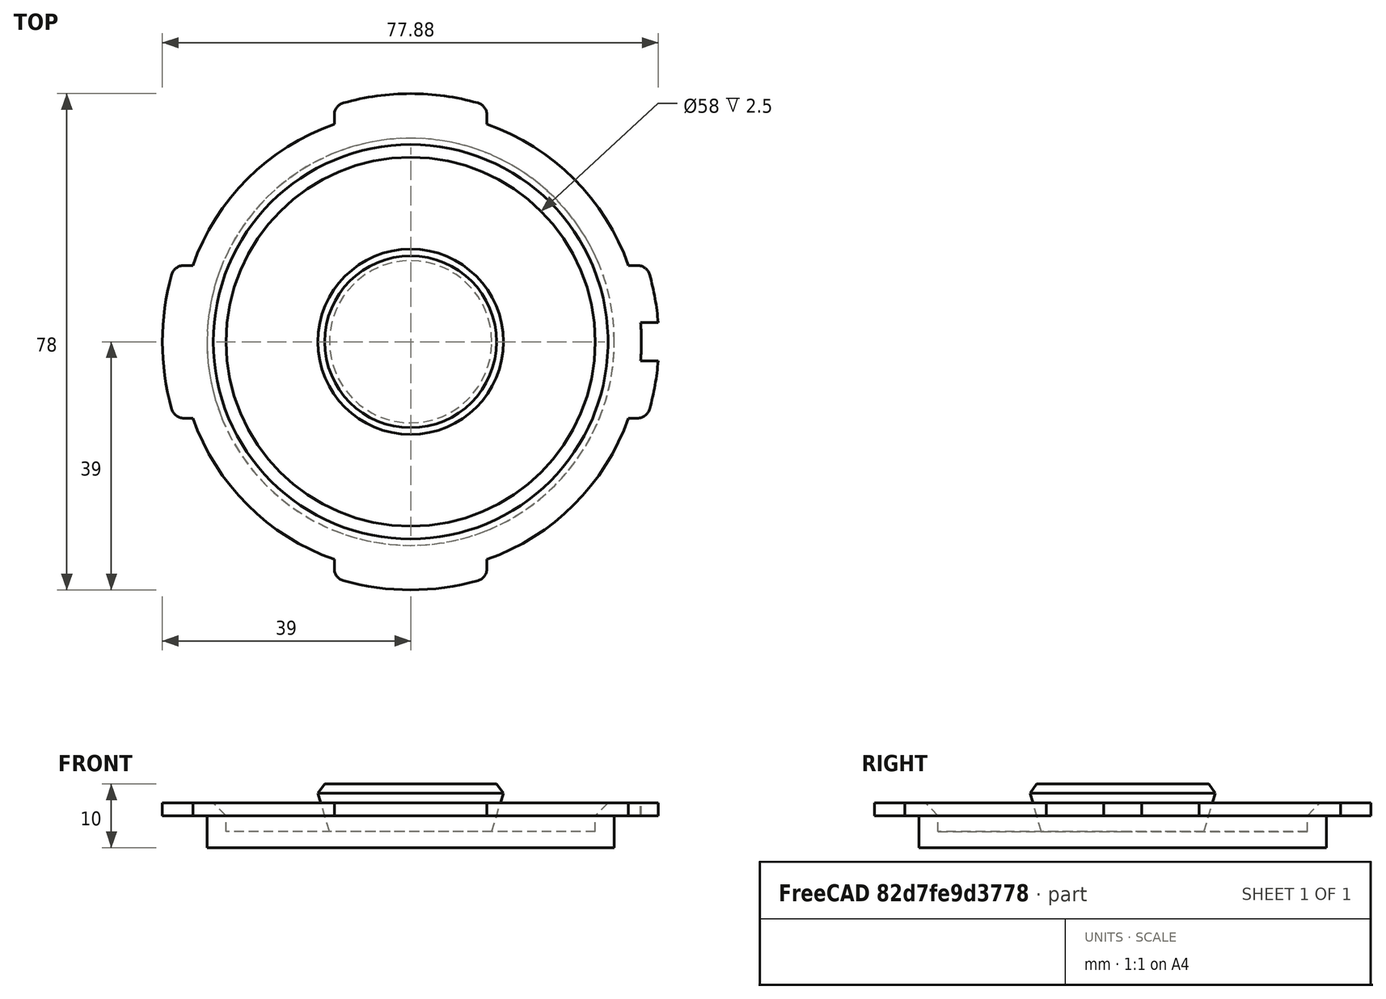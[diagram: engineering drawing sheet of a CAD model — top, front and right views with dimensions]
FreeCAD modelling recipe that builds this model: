
FCSTD DOCUMENT  (FreeCAD 0.18R4 (GitTag))
Label: oct19-body-port-cover
License: All rights reserved
LicenseURL: http://en.wikipedia.org/wiki/All_rights_reserved
objects: Part::Cylinder×6, Part::Box×5, Part::Cut×5, Part::Fillet×4, Part::MultiFuse×4, Part::Fuse×2, Part::Chamfer×2, TechDraw::DrawViewDraft×2, Part::Cone×1, TechDraw::DrawSVGTemplate×1, TechDraw::DrawViewPart×1, TechDraw::DrawViewDimension×1, TechDraw::DrawPage×1
note: 29 computed .brp shape members not serialized (recipe doc carries the construction recipe); baked Part::Feature solids carry a one-line shape summary decoded from their .brp

FEATURE [Part::Cylinder] Cylinder
  Angle = 360
  AttacherType = Attacher::AttachEngine3D
  Height = 7
  Radius = 32
FEATURE [Part::Cylinder] Cylinder001
  Angle = 360
  AttacherType = Attacher::AttachEngine3D
  Height = 2
  Placement = pos=(0,0,5) rot=(0,0,1;0rad)
  Radius = 36.25
FEATURE [Part::Cylinder] Cylinder003
  Angle = 360
  AttacherType = Attacher::AttachEngine3D
  Height = 2
  Placement = pos=(0,0,5) rot=(0,0,1;0rad)
  Radius = 39
FEATURE [Part::Box] Box  label="Cube"
  AttacherType = Attacher::AttachEngine3D
  Height = 10
  Length = 100
  Placement = pos=(-50,12,0) rot=(0,0,1;0rad)
  Width = 40
FEATURE [Part::Box] Box001  label="Cube001"
  AttacherType = Attacher::AttachEngine3D
  Height = 10
  Length = 100
  Placement = pos=(-50,-52,0) rot=(0,0,1;0rad)
  Width = 40
FEATURE [Part::Fuse] Fusion
  Base = -> Box
  Tool = -> Box001
FEATURE [Part::Cut] Cut
  Base = -> Cylinder003
  Tool = -> Fusion
FEATURE [Part::Fillet] Fillet
  Base = -> Cut
  Edges = 2 edges r=2: [Edge3,Edge6]
FEATURE [Part::Fillet] Fillet001
  Base = -> Fillet
  Edges = 2 edges r=2: [Edge19,Edge21]
FEATURE [Part::Box] Box002  label="Cube002"
  AttacherType = Attacher::AttachEngine3D
  Height = 10
  Length = 100
  Placement = pos=(-50,-52,0) rot=(0,0,1;0rad)
  Width = 40
FEATURE [Part::Box] Box003  label="Cube003"
  AttacherType = Attacher::AttachEngine3D
  Height = 10
  Length = 100
  Placement = pos=(-50,12,0) rot=(0,0,1;0rad)
  Width = 40
FEATURE [Part::Fuse] Fusion001
  Base = -> Box003
  Tool = -> Box002
FEATURE [Part::Cylinder] Cylinder004
  Angle = 360
  AttacherType = Attacher::AttachEngine3D
  Height = 2
  Placement = pos=(0,0,5) rot=(0,0,1;0rad)
  Radius = 39
FEATURE [Part::Cut] Cut001
  Base = -> Cylinder004
  Tool = -> Fusion001
FEATURE [Part::Fillet] Fillet003
  Base = -> Cut001
  Edges = 2 edges r=2: [Edge3,Edge6]
FEATURE [Part::Fillet] Fillet002
  Base = -> Fillet003
  Edges = 2 edges r=2: [Edge19,Edge21]
  Placement = pos=(0,0,0) rot=(0,0,1;1.5708rad)
FEATURE [Part::Box] Box004  label="Cube004"
  AttacherType = Attacher::AttachEngine3D
  Height = 10
  Length = 10
  Placement = pos=(36,-3,0) rot=(0,0,1;0rad)
  Width = 6
FEATURE [Part::Cut] Cut002
  Base = -> Fillet001
  Tool = -> Box004
FEATURE [Part::MultiFuse] Fusion002  label="Bayonet"
  Shapes = -> [Fillet002,Cut002]
FEATURE [Part::Cylinder] Cylinder005
  Angle = 360
  AttacherType = Attacher::AttachEngine3D
  Height = 7
  Placement = pos=(0,0,2.5) rot=(0,0,1;0rad)
  Radius = 29
FEATURE [Part::Cylinder] Cylinder006
  Angle = 360
  AttacherType = Attacher::AttachEngine3D
  Height = 7
  Placement = pos=(0,0,4) rot=(0,0,1;0rad)
  Radius = 31
FEATURE [Part::MultiFuse] Fusion003
  Shapes = -> [Cylinder,Fusion002]
FEATURE [Part::MultiFuse] Fusion004
  Shapes = -> [Cylinder001,Fusion003]
FEATURE [Part::Cut] Cut003
  Base = -> Fusion004
  Tool = -> Cylinder005
FEATURE [Part::Chamfer] Chamfer
  Base = -> Cylinder006
  Edges = 1 edges r=3: [Edge3]
FEATURE [Part::Cut] Cut004
  Base = -> Cut003
  Tool = -> Chamfer
FEATURE [Part::Cone] Cone
  Angle = 360
  AttacherType = Attacher::AttachEngine3D
  Height = 10
  Radius1 = 12
  Radius2 = 15
FEATURE [Part::Chamfer] Chamfer001  label="Handle"
  Base = -> Cone
  Edges = 1 edges r=1.5: [Edge1]
FEATURE [Part::MultiFuse] Fusion005  label="oct19-body-port-cover"
  Shapes = -> [Cut004,Chamfer001]
FEATURE [TechDraw::DrawSVGTemplate] Template
  EditableTexts = APPROVER_NAME=APPROVER NAME; AUTHOR_NAME=AUTHOR NAME; DATE=YYYY-MM-DD; DN=DN; OWNER_NAME=OWNER NAME; PM=PM; PN=PN; REVISION=REV A; RIGHTS=(R) DO NOT DUPLICATE THIS DRAWING TO THIRD PARTIES WITHOUT OWNER'S PERMISSION !; SCALE=M x:x; SHEET=99 of 99; SIZE=A4; TITLELINE-1=FreeCAD; TOLERANCE=+/- ?
  Height = 210
  Orientation = 1
  Width = 297
FEATURE [TechDraw::DrawViewDraft] DraftView  label="Front"
  Direction = (0,0,1)
  FontSize = 12
  LineSpacing = 1
  LineStyle = Solie
  LineWidth = 0.35
  LockPosition = false
  Rotation = 0
  ScaleType = 2
  Source = -> Fusion005
  Symbol = <blob: 27096 chars omitted>
  X = 130
  Y = 105
FEATURE [TechDraw::DrawViewDraft] DraftView001  label="Side"
  Direction = (0,1,0)
  FontSize = 12
  LineSpacing = 1
  LineStyle = Solid
  LineWidth = 0.35
  LockPosition = false
  Rotation = 0
  ScaleType = 2
  Source = -> Fusion005
  Symbol = <blob: 34503 chars omitted>
  X = 48.5
  Y = 105
FEATURE [TechDraw::DrawViewPart] View
  CoarseView = false
  Direction = (0.839,-0.133,0.528)
  Focus = 100
  HardHidden = false
  IsoCount = 0
  IsoHidden = false
  IsoVisible = false
  LockPosition = false
  Perspective = false
  Rotation = 0
  ScaleType = 0
  SeamHidden = false
  SeamVisible = false
  SmoothHidden = false
  SmoothVisible = false
  Source = -> [Fusion005]
  X = 230
  Y = 105
FEATURE [TechDraw::DrawViewDimension] Dimension
  Arbitrary = false
  FormatSpec = %.2f
  LockPosition = false
  MeasureType = 1
  OverTolerance = 0
  References2D = -> [View]
  Rotation = 0
  ScaleType = 0
  Type = 1
  UnderTolerance = 0
  X = -2.30066
  Y = 40.4483
FEATURE [TechDraw::DrawPage] Page
  KeepUpdated = true
  ProjectionType = 0
  Template = -> Template
  Views = -> [DraftView,DraftView001,View,Dimension]
